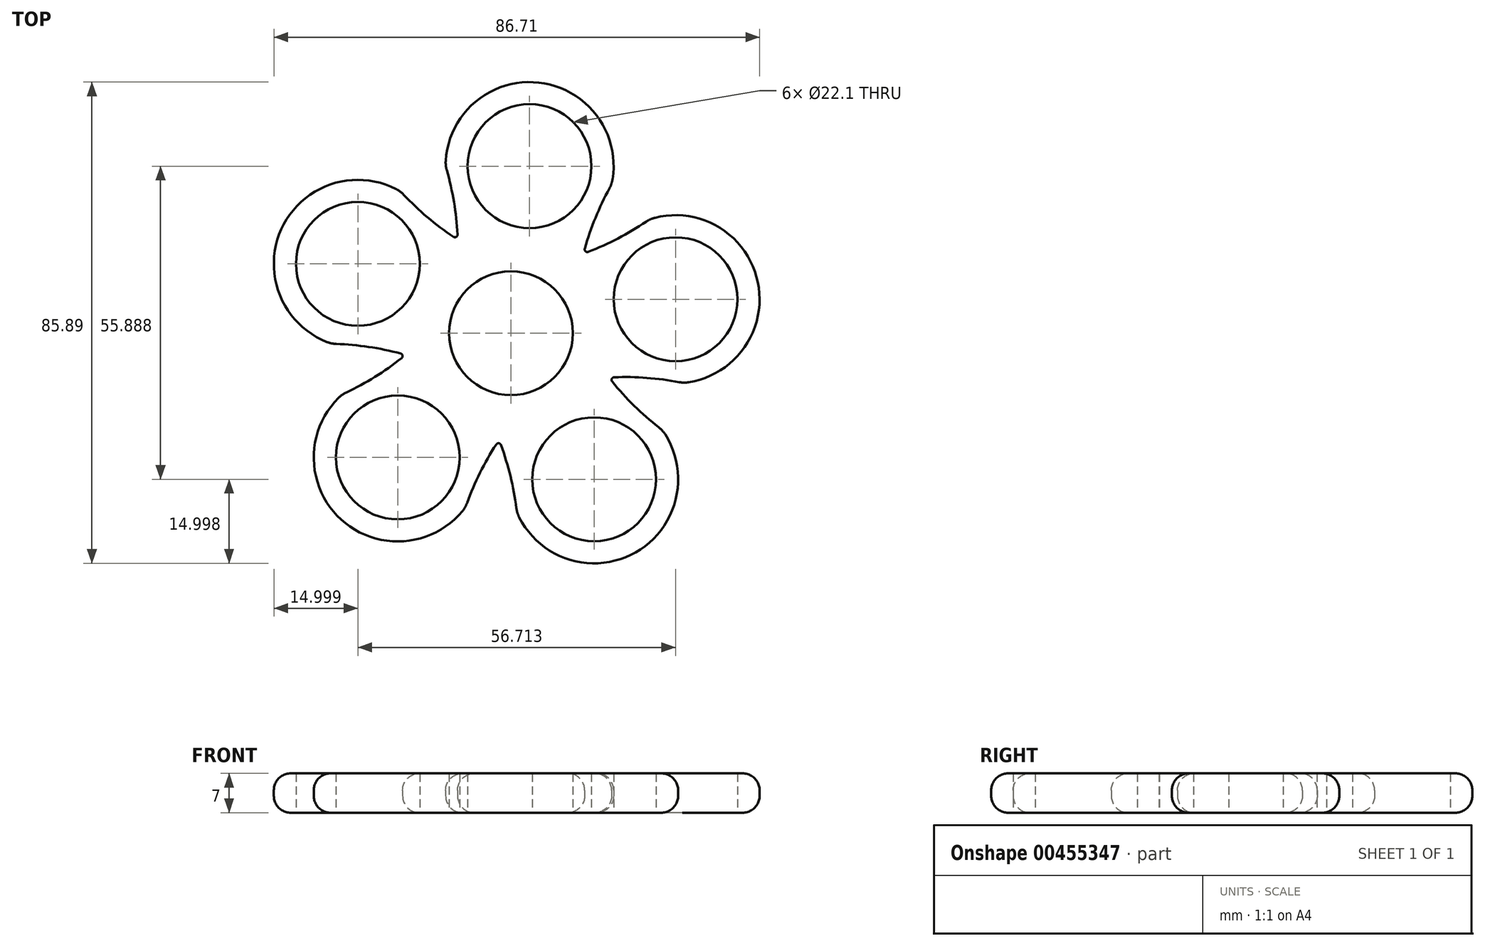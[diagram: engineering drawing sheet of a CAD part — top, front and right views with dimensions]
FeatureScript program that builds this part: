
annotation { "Feature Type Name" : "Feature", "Feature Type Description" : "" }
export const myFeature = defineFeature(function(context is Context, id is Id, definition is map)
    precondition{}
    {
        {
            var Q0;
            Q0=qCreatedBy(makeId("Top.planeOp"),FACE);
            var sketch = newSketch(context, id + "F0", { "sketchPlane" : qUnion([Q0])});
            skCircle(sketch, "E0.cCircle", {"center": v(0, 0) * mm, "radius": 24.27 * mm, "construction": true});
            skPoint(sketch, "E0.0.midPoint", {"position": v(-12, 21.1) * mm});
            skCircle(sketch, "E1", {"center": v(3.32, 29.82) * mm, "radius": 11.05 * mm});
            skCircle(sketch, "E2", {"center": v(0, 0) * mm, "radius": 11.05 * mm});
            skCircle(sketch, "E3", {"center": v(-27.33, 12.37) * mm, "radius": 11.05 * mm});
            skCircle(sketch, "E4", {"center": v(-20.2, -22.17) * mm, "radius": 11.05 * mm});
            skCircle(sketch, "E5", {"center": v(14.84, -26.07) * mm, "radius": 11.05 * mm});
            skCircle(sketch, "E6", {"center": v(29.38, 6.06) * mm, "radius": 11.05 * mm});
            skArc(sketch, "E7", {"start": v(-11.65, 30.79) * mm, "mid": v(3.8, 44.8) * mm, "end": v(18.32, 29.82) * mm});
            skLineSegment(sketch, "E8", {"start": v(3.32, 29.82) * mm, "end": v(-11.68, 29.82) * mm});
            skLineSegment(sketch, "E9", {"start": v(3.32, 29.82) * mm, "end": v(18.32, 29.82) * mm});
            skCircle(sketch, "E10", {"center": v(0, 0) * mm, "radius": 15 * mm});
            skArc(sketch, "E11", {"start": v(-9.54, 17.62) * mm, "mid": v(-10.18, 23.4) * mm, "end": v(-11.47, 29.09) * mm});
            skPoint(sketch, "E12.visualSharp", {"position": v(-11.68, 29.82) * mm});
            skArc(sketch, "E12.filletArc", {"start": v(-11.65, 30.79) * mm, "mid": v(-11.63, 29.93) * mm, "end": v(-11.47, 29.09) * mm});
            skLineSegment(sketch, "E13", {"start": v(0, 0) * mm, "end": v(3.32, 29.82) * mm});
            skLineSegment(sketch, "E14", {"start": v(0, 0) * mm, "end": v(29.38, 6.06) * mm});
            skArc(sketch, "E15.MirrorCS", {"start": v(18.13, 27.47) * mm, "mid": v(6.14, 44.55) * mm, "end": v(-11.31, 33.11) * mm});
            skArc(sketch, "E16.MirrorCS", {"start": v(13.18, 15.09) * mm, "mid": v(15.08, 20.6) * mm, "end": v(17.58, 25.85) * mm});
            skArc(sketch, "E17.MirrorCS", {"start": v(18.13, 27.47) * mm, "mid": v(17.93, 26.64) * mm, "end": v(17.58, 25.85) * mm});
            skArc(sketch, "E18.MirrorCS", {"start": v(18.07, -8.65) * mm, "mid": v(22, -12.95) * mm, "end": v(26.37, -16.8) * mm});
            skArc(sketch, "E19.MirrorCS", {"start": v(-1.8, -19.95) * mm, "mid": v(-0.1, -25.52) * mm, "end": v(0.97, -31.25) * mm});
            skArc(sketch, "E20.MirrorCS", {"start": v(1.48, -32.89) * mm, "mid": v(21.22, -39.65) * mm, "end": v(28.62, -20.14) * mm});
            skArc(sketch, "E21.MirrorCS", {"start": v(1.48, -32.89) * mm, "mid": v(1.16, -32.1) * mm, "end": v(0.97, -31.25) * mm});
            skArc(sketch, "E22.MirrorCS", {"start": v(27.52, -18.06) * mm, "mid": v(27, -17.38) * mm, "end": v(26.37, -16.8) * mm});
            skArc(sketch, "E23.MirrorCS", {"start": v(27.52, -18.06) * mm, "mid": v(23.26, -38.49) * mm, "end": v(2.7, -34.89) * mm});
            skArc(sketch, "E24.MirrorCS", {"start": v(-19.53, -4.46) * mm, "mid": v(-24.3, -7.8) * mm, "end": v(-29.42, -10.58) * mm});
            skArc(sketch, "E25.MirrorCS", {"start": v(-2.64, -19.86) * mm, "mid": v(-5.52, -24.92) * mm, "end": v(-7.82, -30.27) * mm});
            skArc(sketch, "E26.MirrorCS", {"start": v(-8.67, -31.76) * mm, "mid": v(-29.42, -34.01) * mm, "end": v(-32.35, -13.35) * mm});
            skArc(sketch, "E27.MirrorCS", {"start": v(-8.67, -31.76) * mm, "mid": v(-8.18, -31.05) * mm, "end": v(-7.82, -30.27) * mm});
            skArc(sketch, "E28.MirrorCS", {"start": v(-30.82, -11.57) * mm, "mid": v(-30.16, -11.02) * mm, "end": v(-29.42, -10.58) * mm});
            skArc(sketch, "E29.MirrorCS", {"start": v(-30.82, -11.57) * mm, "mid": v(-31.15, -32.43) * mm, "end": v(-10.3, -33.44) * mm});
            skArc(sketch, "E30.MirrorCS", {"start": v(11.87, 9.17) * mm, "mid": v(14.01, 17.76) * mm, "end": v(17.58, 25.85) * mm});
            skArc(sketch, "E31.MirrorCS", {"start": v(-9.56, 11.56) * mm, "mid": v(-9.76, 20.4) * mm, "end": v(-11.47, 29.09) * mm});
            skArc(sketch, "E32.MirrorCS", {"start": v(-13.95, -5.52) * mm, "mid": v(-22.42, -2.98) * mm, "end": v(-31.2, -1.92) * mm});
            skArc(sketch, "E33.MirrorCS", {"start": v(-10.28, 17.2) * mm, "mid": v(-14.93, 20.7) * mm, "end": v(-19.16, 24.71) * mm});
            skArc(sketch, "E34.MirrorCS", {"start": v(-19.7, -3.63) * mm, "mid": v(-25.4, -2.45) * mm, "end": v(-31.2, -1.92) * mm});
            skArc(sketch, "E35.MirrorCS", {"start": v(-32.88, -1.57) * mm, "mid": v(-41.44, 17.47) * mm, "end": v(-22.7, 26.64) * mm});
            skArc(sketch, "E36.MirrorCS", {"start": v(-20.53, 25.74) * mm, "mid": v(-40.47, 19.6) * mm, "end": v(-34.99, -0.53) * mm});
            skArc(sketch, "E37.MirrorCS", {"start": v(-20.53, 25.74) * mm, "mid": v(-19.8, 25.28) * mm, "end": v(-19.16, 24.71) * mm});
            skArc(sketch, "E38.MirrorCS", {"start": v(-32.88, -1.57) * mm, "mid": v(-32.06, -1.81) * mm, "end": v(-31.2, -1.92) * mm});
            skArc(sketch, "E39.MirrorCS", {"start": v(13.8, 14.52) * mm, "mid": v(19.12, 16.91) * mm, "end": v(24.12, 19.9) * mm});
            skArc(sketch, "E40.MirrorCS", {"start": v(18.42, -7.87) * mm, "mid": v(24.25, -7.97) * mm, "end": v(30.02, -8.73) * mm});
            skArc(sketch, "E41.MirrorCS", {"start": v(31.73, -8.76) * mm, "mid": v(44.27, 7.93) * mm, "end": v(28, 21) * mm});
            skArc(sketch, "E42.MirrorCS", {"start": v(31.73, -8.76) * mm, "mid": v(30.88, -8.82) * mm, "end": v(30.02, -8.73) * mm});
            skArc(sketch, "E43.MirrorCS", {"start": v(25.68, 20.6) * mm, "mid": v(43.8, 10.23) * mm, "end": v(34.02, -8.2) * mm});
            skArc(sketch, "E44.MirrorCS", {"start": v(25.68, 20.6) * mm, "mid": v(24.87, 20.31) * mm, "end": v(24.12, 19.9) * mm});
            skPoint(sketch, "E45.newPointA", {"position": v(-5.05, 14.12) * mm});
            skPoint(sketch, "E45.newPointB", {"position": v(-9.56, 11.56) * mm});
            skArc(sketch, "E45.filletArc", {"start": v(-10.28, 17.2) * mm, "mid": v(-9.78, 17.18) * mm, "end": v(-9.54, 17.62) * mm});
            skPoint(sketch, "E46.newPointA", {"position": v(-15, -0.44) * mm});
            skPoint(sketch, "E46.newPointB", {"position": v(-13.95, -5.52) * mm});
            skArc(sketch, "E46.filletArc", {"start": v(-19.53, -4.46) * mm, "mid": v(-19.36, -4) * mm, "end": v(-19.7, -3.63) * mm});
            skPoint(sketch, "E47.newPointA", {"position": v(0.95, -14.97) * mm});
            skPoint(sketch, "E47.newPointB", {"position": v(-4.21, -14.4) * mm});
            skArc(sketch, "E47.filletArc", {"start": v(-1.8, -19.95) * mm, "mid": v(-2.19, -19.64) * mm, "end": v(-2.64, -19.86) * mm});
            skPoint(sketch, "E48.newPointA", {"position": v(14.53, -3.73) * mm});
            skPoint(sketch, "E48.newPointB", {"position": v(12.39, -8.46) * mm});
            skArc(sketch, "E48.filletArc", {"start": v(18.42, -7.87) * mm, "mid": v(18, -8.15) * mm, "end": v(18.07, -8.65) * mm});
            skPoint(sketch, "E49.newPointA", {"position": v(8.03, 12.67) * mm});
            skPoint(sketch, "E49.newPointB", {"position": v(11.87, 9.17) * mm});
            skArc(sketch, "E49.filletArc", {"start": v(13.18, 15.09) * mm, "mid": v(13.32, 14.6) * mm, "end": v(13.8, 14.52) * mm});
            skSolve(sketch);
        }
        {
            var Q0;
            Q0 = qSketchRegion(id + "F0", true);
            var Q1;
            {var subQ5=sQuery(id+"F0.wireOp",EDGE,"E13");var subQ7=sQuery(id+"F0.wireOp",EDGE,"E2");var subQ8=makeQuery(id+"F0.imprint","INTERSECT",VERTEX,{"derivedFrom":[subQ7,subQ5]});Q1=makeQuery(id+"F0.imprint","IMPRINT",FACE,{"disambiguationData":[TD([[makeQuery(id+"F0.imprint","IMPRINT",EDGE,{"disambiguationData":[TD([[subQ8,-1.0]])],"derivedFrom":subQ7}),-1.0]])]});}
            var Q2;
            {var subQ0=sQuery(id+"F0.wireOp",EDGE,"E13");var subQ1=sQuery(id+"F0.wireOp",EDGE,"E2");var subQ2=makeQuery(id+"F0.imprint","INTERSECT",VERTEX,{"derivedFrom":[subQ1,subQ0]});Q2=makeQuery(id+"F0.imprint","IMPRINT",FACE,{"disambiguationData":[TD([[makeQuery(id+"F0.imprint","IMPRINT",EDGE,{"disambiguationData":[TD([[subQ2,1.0]])],"derivedFrom":subQ1}),-1.0]])]});}
            extrude(context, id + "F1", {"entities" : qUnion([Q0, Q1, Q2]), "depth" : 7 * mm});
        }
        {
            var Q0;
            Q0=makeQuery(id+"F1.opExtrude","CAP_EDGE",EDGE,{"disambiguationData":[OSD([sQuery(id+"F0.wireOp",EDGE,"E7"),sQuery(id+"F0.wireOp",EDGE,"E15.MirrorCS")])],"isStart":false});
            var Q1;
            Q1=makeQuery(id+"F1.opExtrude","CAP_EDGE",EDGE,{"disambiguationData":[OSD([sQuery(id+"F0.wireOp",EDGE,"E35.MirrorCS"),sQuery(id+"F0.wireOp",EDGE,"E36.MirrorCS")])],"isStart":false});
            fillet(context, id + "F2", {"entities" : qUnion([Q0, Q1]), "radius" : 3 * mm, "tangentPropagation" : true, "allowEdgeOverflow" : false});
        }
        {
            var Q0;
            Q0=makeQuery(id+"F1.opExtrude","CAP_EDGE",EDGE,{"disambiguationData":[OSD([sQuery(id+"F0.wireOp",EDGE,"E35.MirrorCS"),sQuery(id+"F0.wireOp",EDGE,"E36.MirrorCS")])],"isStart":true});
            var Q1;
            Q1=makeQuery(id+"F1.opExtrude","CAP_EDGE",EDGE,{"disambiguationData":[OSD([sQuery(id+"F0.wireOp",EDGE,"E26.MirrorCS"),sQuery(id+"F0.wireOp",EDGE,"E29.MirrorCS")])],"isStart":true});
            fillet(context, id + "F3", {"entities" : qUnion([Q0, Q1]), "radius" : 3 * mm, "tangentPropagation" : true, "allowEdgeOverflow" : false});
        }
    });
